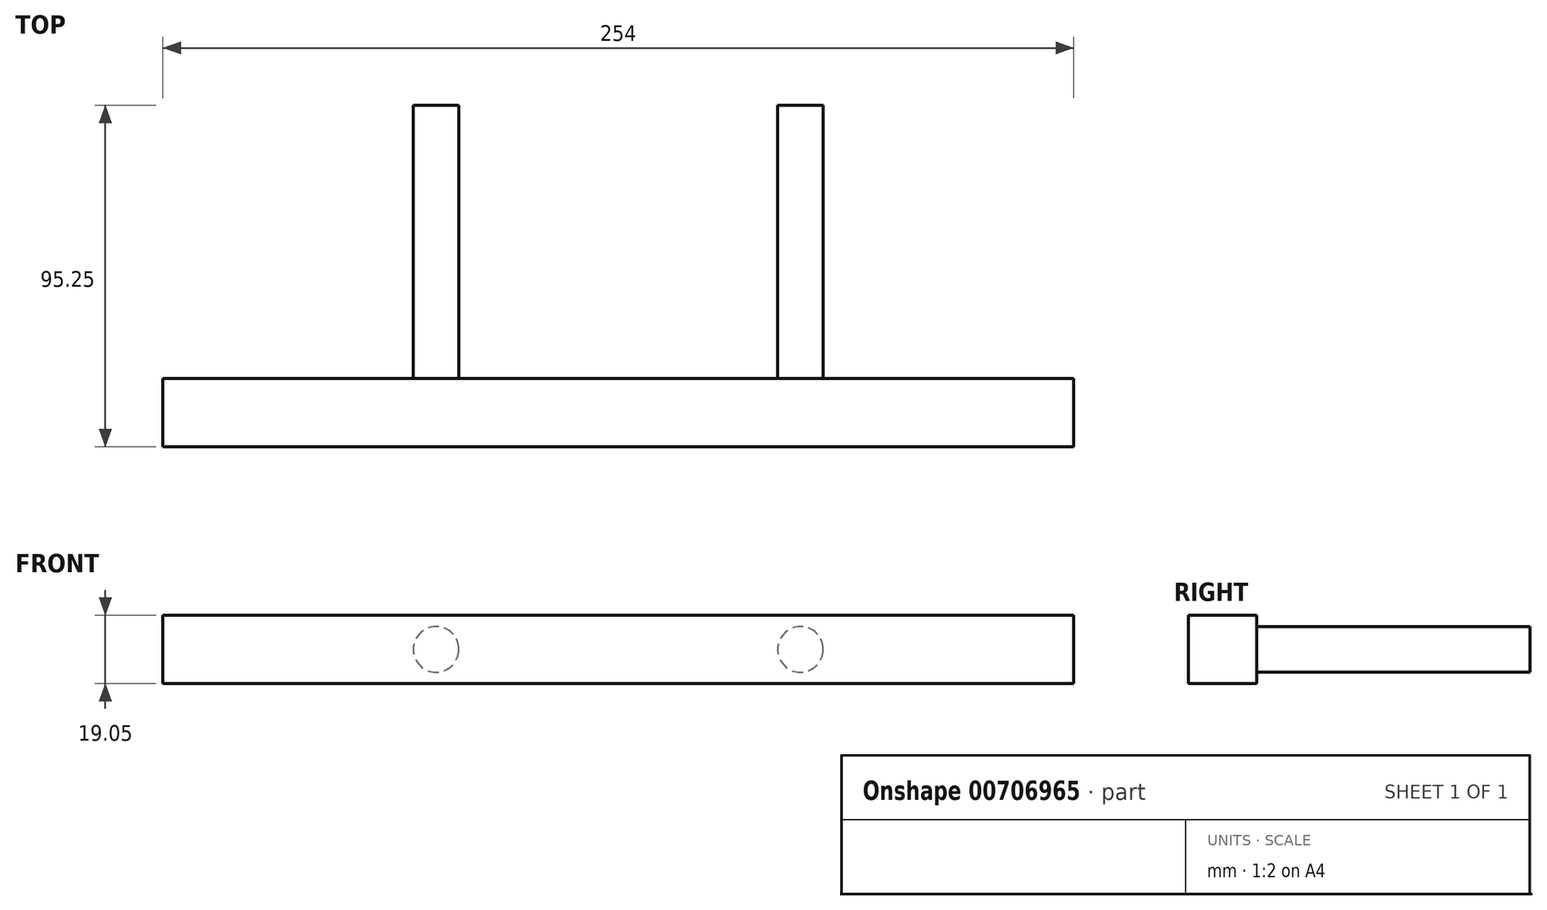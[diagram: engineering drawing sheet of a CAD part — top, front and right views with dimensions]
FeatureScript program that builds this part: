
annotation { "Feature Type Name" : "Feature", "Feature Type Description" : "" }
export const myFeature = defineFeature(function(context is Context, id is Id, definition is map)
    precondition{}
    {
        {
            var Q0;
            Q0=qCreatedBy(makeId("Front.planeOp"),FACE);
            var sketch = newSketch(context, id + "F0", { "sketchPlane" : qUnion([Q0])});
            skLineSegment(sketch, "E0.bottom", {"start": v(127, 0) * mm, "end": v(-127, 0) * mm});
            skLineSegment(sketch, "E0.top", {"start": v(127, 19.05) * mm, "end": v(-127, 19.05) * mm});
            skLineSegment(sketch, "E0.left", {"start": v(127, 0) * mm, "end": v(127, 19.05) * mm});
            skLineSegment(sketch, "E0.right", {"start": v(-127, 0) * mm, "end": v(-127, 19.05) * mm});
            skSolve(sketch);
        }
        {
            var Q0;
            Q0=makeQuery(id+"F0.imprint","IMPRINT",FACE,{"disambiguationData":[TD([[makeQuery(id+"F0.imprint","IMPRINT",EDGE,{"derivedFrom":sQuery(id+"F0.wireOp",EDGE,"E0.bottom")}),-1.0]])]});
            var sketch = newSketch(context, id + "F1", { "sketchPlane" : qUnion([Q0])});
            skSolve(sketch);
        }
        {
            var Q0;
            Q0=makeQuery(id+"F1.imprint","IMPRINT",FACE,{"disambiguationData":[TD([[makeQuery(id+"F1.imprint","IMPRINT",EDGE,{"derivedFrom":makeQuery(id+"F0.imprint","IMPRINT",EDGE,{"derivedFrom":sQuery(id+"F0.wireOp",EDGE,"E0.bottom")})}),-1.0]])]});
            extrude(context, id + "F2", {"entities" : qUnion([Q0]), "depth" : 19.05 * mm, "offsetDistance" : 25.4 * mm});
        }
        {
            var Q0;
            Q0=qCreatedBy(makeId("Front.planeOp"),FACE);
            var sketch = newSketch(context, id + "F3", { "sketchPlane" : qUnion([Q0])});
            skCircle(sketch, "E1", {"center": v(-50.8, 9.52) * mm, "radius": 6.35 * mm});
            skCircle(sketch, "E2", {"center": v(50.8, 9.53) * mm, "radius": 6.35 * mm});
            skSolve(sketch);
        }
        {
            var Q0;
            Q0=makeQuery(id+"F3.imprint","IMPRINT",FACE,{"disambiguationData":[TD([[makeQuery(id+"F3.imprint","IMPRINT",EDGE,{"derivedFrom":sQuery(id+"F3.wireOp",EDGE,"E2")}),1.0]])]});
            var Q1;
            Q1=makeQuery(id+"F3.imprint","IMPRINT",FACE,{"disambiguationData":[TD([[makeQuery(id+"F3.imprint","IMPRINT",EDGE,{"derivedFrom":sQuery(id+"F3.wireOp",EDGE,"E1")}),1.0]])]});
            extrude(context, id + "F4", {"entities" : qUnion([Q0, Q1]), "oppositeDirection" : true, "depth" : 76.2 * mm, "offsetDistance" : 25.4 * mm});
        }
    });
